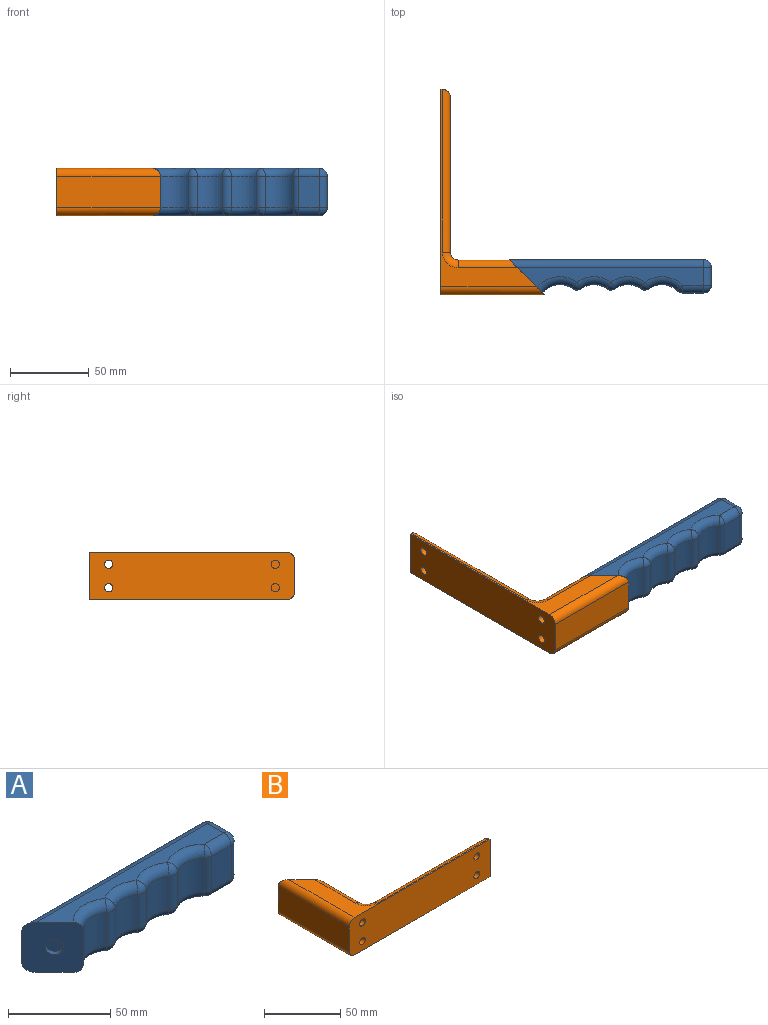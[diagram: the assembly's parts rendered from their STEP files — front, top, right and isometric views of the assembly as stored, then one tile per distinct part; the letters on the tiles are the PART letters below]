
ASSEMBLY  parts=2 mates=1
PART A: 46 faces, bbox 128.6x21.5x30.2 mm
  f0: cylinder r=4.5mm len=9mm, axis (-0.71,-0.71,0), area 84.8mm2, adj f1,f9
  f1: plane 14x9.9mm, normal (0.71,0.71,0), area 90.3mm2, adj f0,f3
  f2: plane 14x9.9mm, normal (-0.71,-0.71,0), area 153.9mm2, adj f3
  f3: cylinder r=7mm len=14mm, axis (-0.71,-0.71,0), area 175.9mm2, adj f1,f2
  f4: torus R=18.66mm, axis (0,0,1), area 184.2mm2, adj f8,f9,f18,f31
  f5: cylinder r=5mm len=20mm, axis (0,0,1), area 123.7mm2, adj f6,f10,f29,f35
  f6: cylinder r=13.66mm len=20mm, axis (0,0,1), area 338.2mm2, adj f5,f7,f28,f36
  f7: cylinder r=5mm len=20mm, axis (0,0,1), area 123.7mm2, adj f6,f12,f27,f37
  f8: cylinder r=13.66mm len=20mm, axis (0,0,1), area 419mm2, adj f4,f9,f11,f32
  f9: plane 30.16x21.45mm, normal (-0.71,-0.71,0), area 813.8mm2, adj f0,f4,f8,f11,f16,f18,f19,f44
  f10: cylinder r=13.66mm len=20mm, axis (0,0,1), area 338.2mm2, adj f5,f30,f32,f34
  f11: torus R=18.66mm, axis (0,0,1), area 184.2mm2, adj f8,f9,f19,f33
  f12: cylinder r=13.66mm len=20mm, axis (0,0,1), area 380.8mm2, adj f7,f13,f26,f38
  f13: cylinder r=5mm len=20mm, axis (0,0,1), area 77.5mm2, adj f12,f14,f25,f39
  f14: plane 20x13.31mm, normal (0,-1,0), area 266.1mm2, adj f13,f15,f24,f40
  f15: cylinder r=5mm len=20mm, axis (0,0,-1), area 157.1mm2, adj f14,f17,f23,f41
  f16: plane 123.43x20mm, normal (0,1,0), area 2468.6mm2, adj f9,f20,f44,f45
  f17: plane 20x11.29mm, normal (1,0,0), area 225.9mm2, adj f15,f20,f22,f42
  f18: plane 118.43x12.74mm, normal (0,0,1), area 905.9mm2, adj f4,f9,f22,f24,f26,f28,f30,f45
  f19: plane 118.43x12.74mm, normal (0,0,-1), area 905.9mm2, adj f9,f11,f34,f36,f38,f40,f42,f44
  f20: cylinder r=5mm len=20mm, axis (0,0,-1), area 157.1mm2, adj f16,f17,f21,f43
  f21: sphere r=5mm, area 39.3mm2, adj f20,f22,f45
  f22: cylinder r=5mm len=11.29mm, axis (0,-1,0), area 88.7mm2, adj f17,f18,f21,f23
  f23: sphere r=5mm, area 39.3mm2, adj f15,f22,f24
  f24: cylinder r=5mm len=13.31mm, axis (1,0,0), area 104.5mm2, adj f14,f18,f23,f25
  f25: sphere r=5mm, area 19.4mm2, adj f13,f24,f26
  f26: torus R=18.66mm, axis (0,0,1), area 169.4mm2, adj f12,f18,f25,f27
  f27: sphere r=5mm, area 30.9mm2, adj f7,f26,f28
  f28: torus R=18.66mm, axis (0,0,1), area 150.5mm2, adj f6,f18,f27,f29
  f29: sphere r=5mm, area 30.9mm2, adj f5,f28,f30
  f30: torus R=18.66mm, axis (0,0,1), area 150.5mm2, adj f10,f18,f29,f31
  f31: sphere r=5mm, area 31.9mm2, adj f4,f30,f32
  f32: cylinder r=5mm len=20mm, axis (0,0,1), area 123.7mm2, adj f8,f10,f31,f33
  f33: sphere r=5mm, area 30.9mm2, adj f11,f32,f34
  f34: torus R=18.66mm, axis (0,0,1), area 150.5mm2, adj f10,f19,f33,f35
  f35: sphere r=5mm, area 30.9mm2, adj f5,f34,f36
  f36: torus R=18.66mm, axis (0,0,1), area 150.5mm2, adj f6,f19,f35,f37
  f37: sphere r=5mm, area 30.9mm2, adj f7,f36,f38
  f38: torus R=18.66mm, axis (0,0,1), area 169.4mm2, adj f12,f19,f37,f39
  f39: sphere r=5mm, area 19.4mm2, adj f13,f38,f40
  f40: cylinder r=5mm len=13.31mm, axis (1,0,0), area 104.5mm2, adj f14,f19,f39,f41
  f41: sphere r=5mm, area 39.3mm2, adj f15,f40,f42
  f42: cylinder r=5mm len=11.29mm, axis (0,-1,0), area 88.7mm2, adj f17,f19,f41,f43
  f43: sphere r=5mm, area 39.3mm2, adj f20,f42,f44
  f44: cylinder r=5mm len=123.43mm, axis (1,0,0), area 955.1mm2, adj f9,f16,f19,f43
  f45: cylinder r=5mm len=123.43mm, axis (1,0,0), area 955.1mm2, adj f9,f16,f18,f21
PART B: 28 faces, bbox 130.6x69.7x30 mm
  f0: plane 13x9.19mm, normal (-0.71,-0.71,0), area 82.5mm2, adj f2,f3
  f1: plane 13x9.19mm, normal (0.71,0.71,0), area 132.7mm2, adj f2
  f2: cylinder r=6.5mm len=13mm, axis (0.71,0.71,0), area 122.5mm2, adj f0,f1
  f3: cylinder r=4mm len=8.49mm, axis (0.71,0.71,0), area 100.5mm2, adj f0,f20
  f4: cylinder r=2.65mm len=6mm, axis (0,-1,0), area 99.9mm2, adj f12,f23,f25
  f5: cylinder r=2.65mm len=6mm, axis (0,-1,0), area 99.9mm2, adj f12,f25,f26
  f6: cylinder r=2.65mm len=16.5mm, axis (0,-1,0), area 274.7mm2, adj f8,f12
  f7: cylinder r=2.65mm len=16.5mm, axis (0,-1,0), area 274.7mm2, adj f9,f12
  f8: plane 5.3x5.3mm, normal (0,-1,0), area 22.1mm2, adj f6
  f9: plane 5.3x5.3mm, normal (0,-1,0), area 22.1mm2, adj f7
  f10: cylinder r=5mm len=66mm, axis (0,1,0), area 504.1mm2, adj f11,f12,f14,f20
  f11: plane 66x20mm, normal (-1,0,0), area 1320mm2, adj f10,f12,f13,f20
  f12: plane 130.6x30mm, normal (0,-1,0), area 3819mm2, adj f4,f5,f6,f7,f10,f11,f13,f14
  f13: cylinder r=5mm len=66mm, axis (0,1,0), area 504.1mm2, adj f11,f12,f17,f20
  f14: plane 125.6x61mm, normal (0,0,1), area 795.1mm2, adj f10,f12,f15,f16,f20,f23,f24
  f15: torus R=10mm, axis (0,0,1), area 84.1mm2, adj f14,f16,f19,f23
  f16: cylinder r=5mm len=38mm, axis (0,1,0), area 273.5mm2, adj f14,f15,f18,f20
  f17: plane 125.6x61mm, normal (0,0,-1), area 795.1mm2, adj f12,f13,f20,f21,f22,f24,f26
  f18: plane 33x20mm, normal (1,0,0), area 660mm2, adj f16,f19,f20,f22
  f19: cylinder r=5mm len=20mm, axis (0,0,-1), area 157.1mm2, adj f15,f18,f21,f25
  f20: plane 30x22mm, normal (0.71,0.71,0), area 852.8mm2, adj f3,f10,f11,f13,f14,f16,f17,f18
  f21: torus R=10mm, axis (0,0,1), area 84.1mm2, adj f17,f19,f22,f26
  f22: cylinder r=5mm len=38mm, axis (0,1,0), area 273.5mm2, adj f17,f18,f20,f21
  f23: cylinder r=5mm len=103.6mm, axis (-1,0,0), area 799.4mm2, adj f4,f14,f15,f25,f27
  f24: plane 30x1mm, normal (1,0,0), area 30mm2, adj f12,f14,f17,f27
  f25: plane 98.6x20mm, normal (0,1,0), area 1928.2mm2, adj f4,f5,f19,f23,f26,f27
  f26: cylinder r=5mm len=103.6mm, axis (-1,0,0), area 799.4mm2, adj f5,f17,f21,f25,f27
  f27: cylinder r=5mm len=30mm, axis (0,0,-1), area 207.1mm2, adj f23,f24,f25,f26
PLACE A t=(-83.83,5.5,19.25)mm
PLACE B rot(axis=(-0.71,-0.71,0),180deg) t=(-125.39,47.77,19.25)mm
MATE revolute B.f2 <-> A.f3  axis (0.71,0.71,0) through (-132.13,-0.89,19.25)mm
